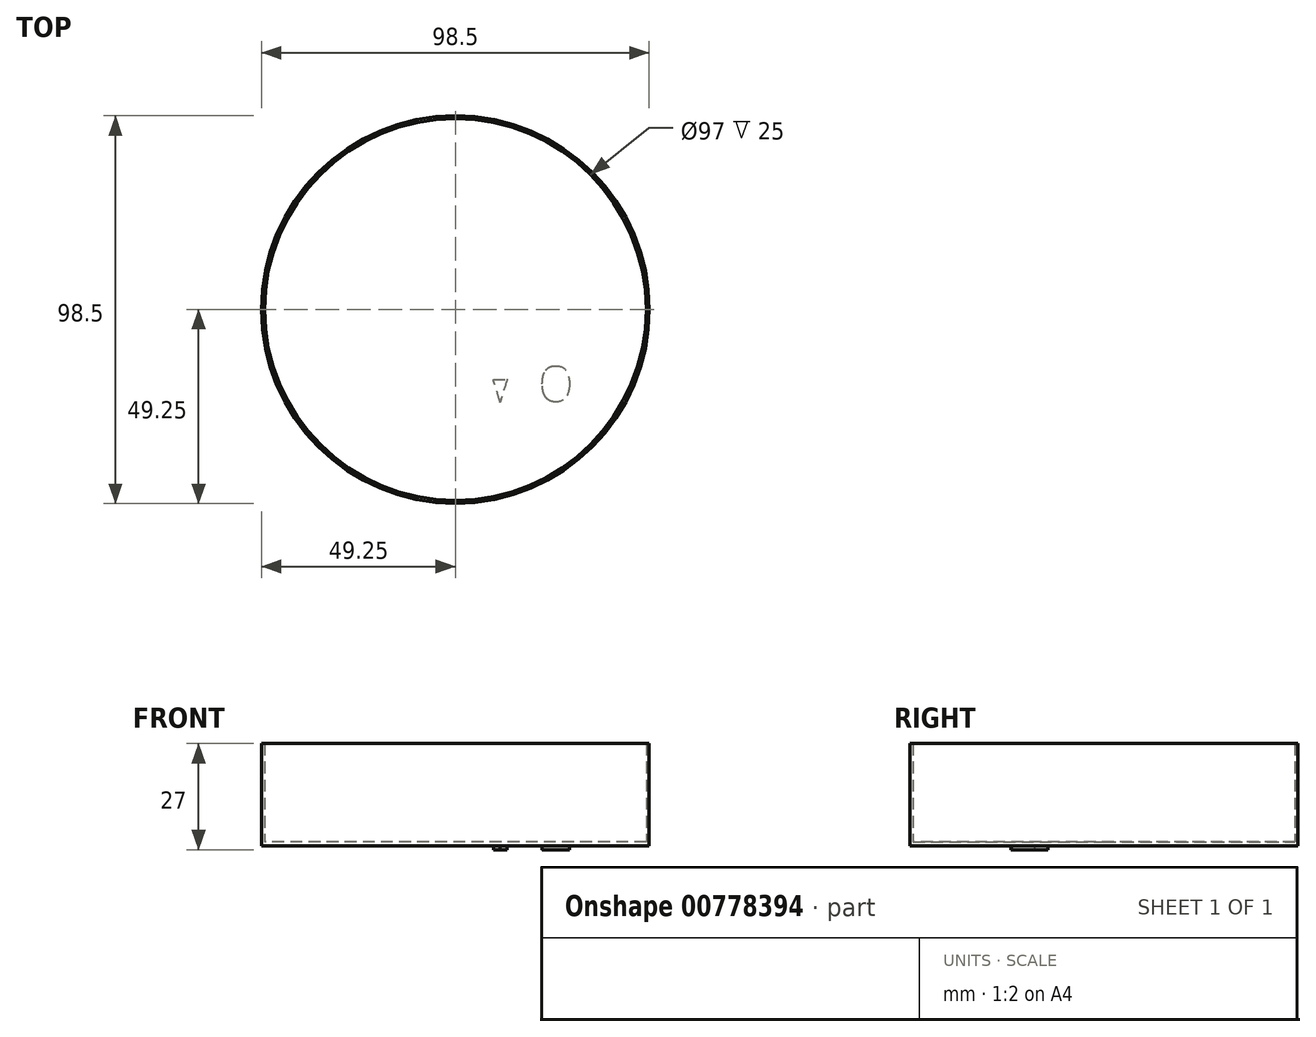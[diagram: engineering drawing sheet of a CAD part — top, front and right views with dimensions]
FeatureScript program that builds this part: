
annotation { "Feature Type Name" : "Feature", "Feature Type Description" : "" }
export const myFeature = defineFeature(function(context is Context, id is Id, definition is map)
    precondition{}
    {
        {
            var Q0;
            Q0=qCreatedBy(makeId("Top.planeOp"),FACE);
            var sketch = newSketch(context, id + "F0", { "sketchPlane" : qUnion([Q0])});
            skCircle(sketch, "E0", {"center": v(0, 0) * mm, "radius": 48.5 * mm});
            skCircle(sketch, "E1", {"center": v(0, 0) * mm, "radius": 49.25 * mm});
            skSolve(sketch);
        }
        {
            var Q0;
            Q0=makeQuery(id+"F0.imprint","IMPRINT",FACE,{"disambiguationData":[TD([[makeQuery(id+"F0.imprint","IMPRINT",EDGE,{"derivedFrom":sQuery(id+"F0.wireOp",EDGE,"E0")}),-1.0]])]});
            var Q1;
            Q1=makeQuery(id+"F0.imprint","IMPRINT",FACE,{"disambiguationData":[TD([[makeQuery(id+"F0.imprint","IMPRINT",EDGE,{"derivedFrom":sQuery(id+"F0.wireOp",EDGE,"E0")}),1.0]])]});
            extrude(context, id + "F1", {"entities" : qUnion([Q0, Q1]), "depth" : -2 * mm, "offsetDistance" : 25.4 * mm});
        }
        {
            var Q0;
            Q0=makeQuery(id+"F0.imprint","IMPRINT",FACE,{"disambiguationData":[TD([[makeQuery(id+"F0.imprint","IMPRINT",EDGE,{"derivedFrom":sQuery(id+"F0.wireOp",EDGE,"E0")}),-1.0]])]});
            extrude(context, id + "F2", {"entities" : qUnion([Q0]), "operationType" : NewBodyOperationType.ADD, "depth" : 25 * mm, "offsetDistance" : 25.4 * mm});
        }
        {
            var Q0;
            Q0=makeQuery(id+"F1.opExtrude","CAP_FACE",FACE,{"disambiguationData":[OSD([sQuery(id+"F0.wireOp",EDGE,"E1")])],"isStart":false});
            var sketch = newSketch(context, id + "F3", { "sketchPlane" : qUnion([Q0])});
            skText(sketch, "E2", { "text": "NIKÃO", "fontName": "OpenSans-Bold.ttf"});
            const initialGuessF3  = {"E2": [-0.02999, 0.01206, 1, 0, 0.0137]};
            skSetInitialGuess(sketch, initialGuessF3);
            skSolve(sketch);
        }
        {
            var Q0;
            Q0=makeQuery(id+"F3.imprint","IMPRINT",FACE,{"disambiguationData":[TD([[makeQuery(id+"F3.imprint","IMPRINT",EDGE,{"derivedFrom":sQuery(id+"F3.wireOp",EDGE,"E2.sketch_text.stroke-0")}),-1.0]])]});
            var Q1;
            Q1=makeQuery(id+"F3.imprint","IMPRINT",FACE,{"disambiguationData":[TD([[makeQuery(id+"F3.imprint","IMPRINT",EDGE,{"derivedFrom":sQuery(id+"F3.wireOp",EDGE,"E2.sketch_text.stroke-14")}),-1.0]])]});
            var Q2;
            Q2=makeQuery(id+"F3.imprint","IMPRINT",FACE,{"disambiguationData":[TD([[makeQuery(id+"F3.imprint","IMPRINT",EDGE,{"derivedFrom":sQuery(id+"F3.wireOp",EDGE,"E2.sketch_text.stroke-18")}),-1.0]])]});
            var Q3;
            Q3=makeQuery(id+"F3.imprint","IMPRINT",FACE,{"disambiguationData":[TD([[makeQuery(id+"F3.imprint","IMPRINT",EDGE,{"derivedFrom":sQuery(id+"F3.wireOp",EDGE,"E2.sketch_text.stroke-31")}),-1.0]])]});
            var Q4;
            Q4=makeQuery(id+"F3.imprint","IMPRINT",FACE,{"disambiguationData":[TD([[makeQuery(id+"F3.imprint","IMPRINT",EDGE,{"derivedFrom":sQuery(id+"F3.wireOp",EDGE,"E2.sketch_text.stroke-43")}),-1.0]])]});
            var Q5;
            Q5=makeQuery(id+"F3.imprint","IMPRINT",FACE,{"disambiguationData":[TD([[makeQuery(id+"F3.imprint","IMPRINT",EDGE,{"derivedFrom":sQuery(id+"F3.wireOp",EDGE,"E2.sketch_text.stroke-61")}),-1.0]])]});
            var Q6;
            Q6=makeQuery(id+"F3.imprint","IMPRINT",FACE,{"disambiguationData":[TD([[makeQuery(id+"F3.imprint","IMPRINT",EDGE,{"derivedFrom":sQuery(id+"F3.wireOp",EDGE,"E2.sketch_text.stroke-0")}),1.0]])]});
            extrude(context, id + "F4", {"entities" : qUnion([Q0, Q1, Q2, Q3, Q4, Q5, Q6]), "operationType" : NewBodyOperationType.REMOVE, "oppositeDirection" : true, "depth" : 1 * mm, "offsetDistance" : 25.4 * mm});
        }
    });
